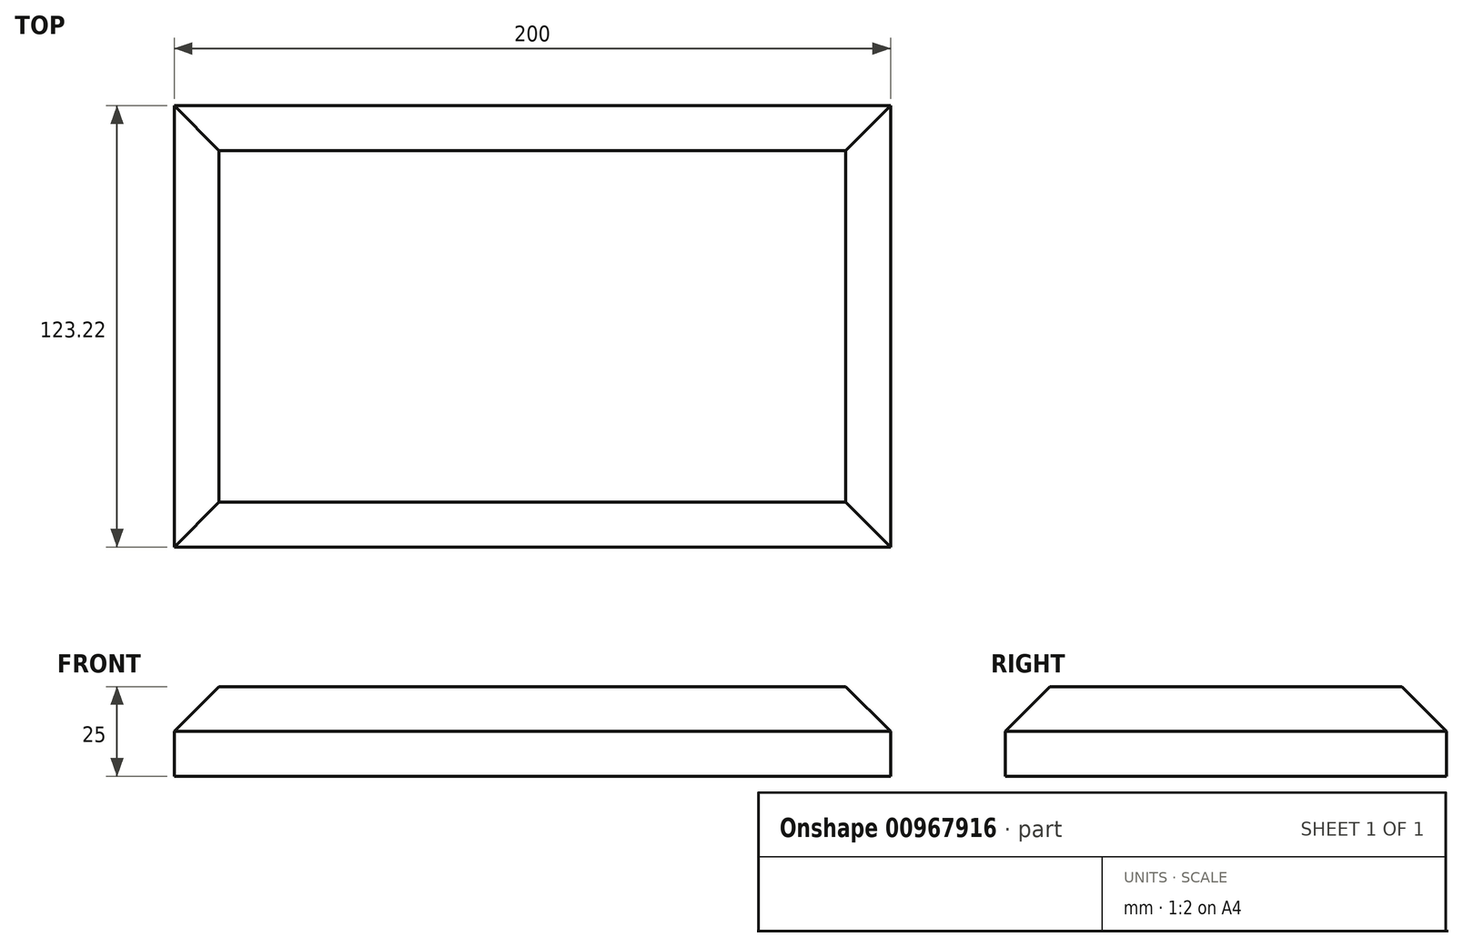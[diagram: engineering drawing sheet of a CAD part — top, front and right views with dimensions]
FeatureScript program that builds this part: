
annotation { "Feature Type Name" : "Feature", "Feature Type Description" : "" }
export const myFeature = defineFeature(function(context is Context, id is Id, definition is map)
    precondition{}
    {
        {
            var Q0;
            Q0=qCreatedBy(makeId("Top.planeOp"),FACE);
            var sketch = newSketch(context, id + "F0", { "sketchPlane" : qUnion([Q0])});
            skLineSegment(sketch, "E0.bottom", {"start": v(-100, 61.61) * mm, "end": v(100, 61.61) * mm});
            skLineSegment(sketch, "E0.top", {"start": v(-100, -61.61) * mm, "end": v(100, -61.61) * mm});
            skLineSegment(sketch, "E0.left", {"start": v(-100, 61.61) * mm, "end": v(-100, -61.61) * mm});
            skLineSegment(sketch, "E0.right", {"start": v(100, 61.61) * mm, "end": v(100, -61.61) * mm});
            skPoint(sketch, "E0.middle", {"position": v(0, 0) * mm});
            skSolve(sketch);
        }
        {
            var Q0;
            Q0=makeQuery(id+"F0.imprint","IMPRINT",FACE,{"disambiguationData":[TD([[makeQuery(id+"F0.imprint","IMPRINT",EDGE,{"derivedFrom":sQuery(id+"F0.wireOp",EDGE,"E0.bottom")}),-1.0]])]});
            extrude(context, id + "F1", {"entities" : qUnion([Q0]), "depth" : 25 * mm, "offsetDistance" : 25 * mm});
        }
        {
            var Q0;
            Q0=makeQuery(id+"F1.opExtrude","CAP_EDGE",EDGE,{"disambiguationData":[OSD([sQuery(id+"F0.wireOp",EDGE,"E0.top")])],"isStart":false});
            var Q1;
            Q1=makeQuery(id+"F1.opExtrude","CAP_EDGE",EDGE,{"disambiguationData":[OSD([sQuery(id+"F0.wireOp",EDGE,"E0.left")])],"isStart":false});
            var Q2;
            Q2=makeQuery(id+"F1.opExtrude","CAP_EDGE",EDGE,{"disambiguationData":[OSD([sQuery(id+"F0.wireOp",EDGE,"E0.bottom")])],"isStart":false});
            var Q3;
            Q3=makeQuery(id+"F1.opExtrude","CAP_EDGE",EDGE,{"disambiguationData":[OSD([sQuery(id+"F0.wireOp",EDGE,"E0.right")])],"isStart":false});
            chamfer(context, id + "F2", {"entities" : qUnion([Q0, Q1, Q2, Q3]), "width" : 12.5 * mm, "tangentPropagation" : true});
        }
    });
